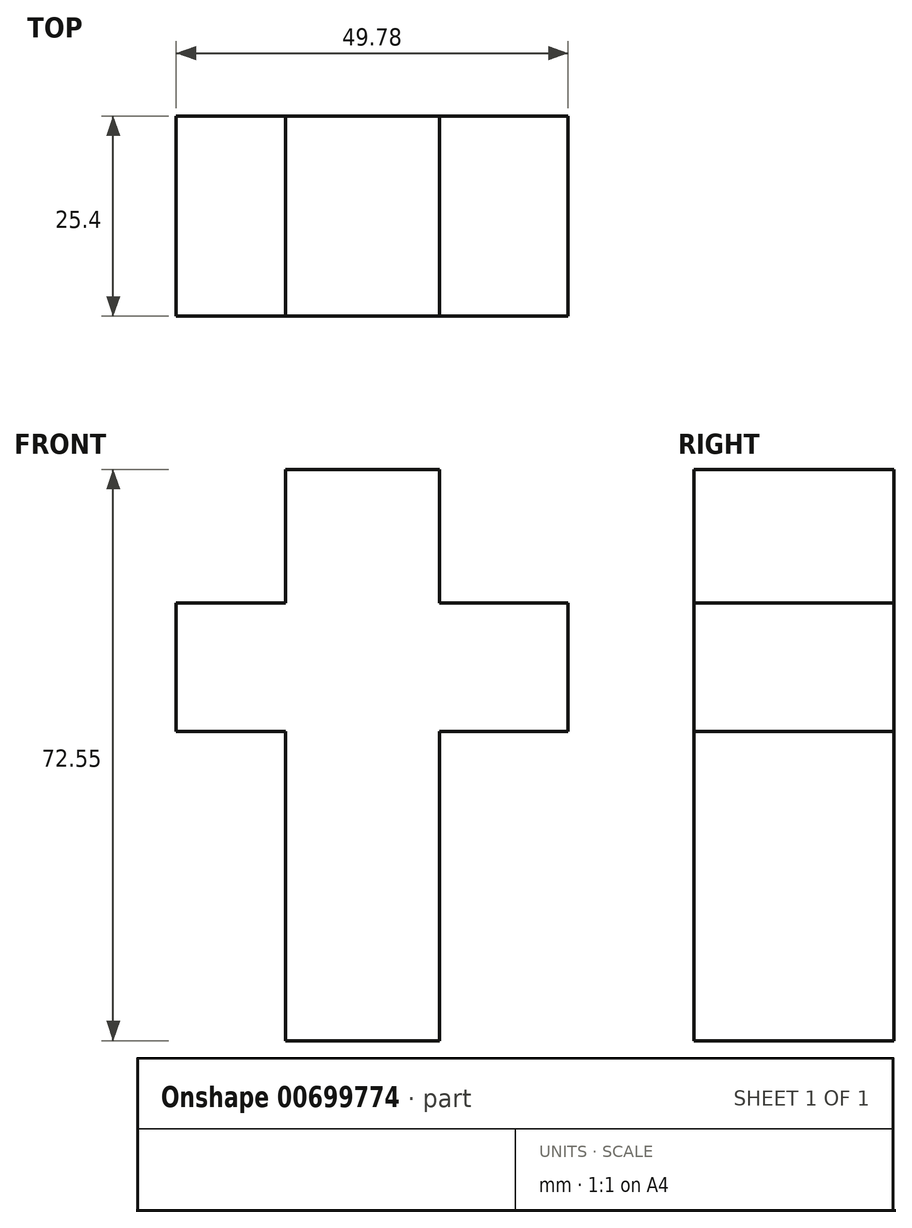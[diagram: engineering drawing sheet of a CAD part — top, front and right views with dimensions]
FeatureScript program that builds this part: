
annotation { "Feature Type Name" : "Feature", "Feature Type Description" : "" }
export const myFeature = defineFeature(function(context is Context, id is Id, definition is map)
    precondition{}
    {
        {
            var Q0;
            Q0=qCreatedBy(makeId("Front.planeOp"),FACE);
            var sketch = newSketch(context, id + "F0", { "sketchPlane" : qUnion([Q0])});
            skLineSegment(sketch, "E0", {"start": v(-29.12, 0) * mm, "end": v(-29.12, -22.87) * mm});
            skLineSegment(sketch, "E1", {"start": v(-29.12, -22.87) * mm, "end": v(-9.57, -22.87) * mm});
            skLineSegment(sketch, "E2", {"start": v(-9.57, -23.08) * mm, "end": v(-9.57, 0) * mm});
            skLineSegment(sketch, "E3", {"start": v(-9.57, 0) * mm, "end": v(-9.57, 16.43) * mm});
            skLineSegment(sketch, "E4", {"start": v(-9.57, 16.43) * mm, "end": v(6.75, 16.43) * mm});
            skLineSegment(sketch, "E5", {"start": v(6.75, 16.43) * mm, "end": v(6.75, 28.11) * mm});
            skLineSegment(sketch, "E6", {"start": v(6.75, 28.11) * mm, "end": v(6.75, 32.75) * mm});
            skLineSegment(sketch, "E7", {"start": v(6.75, 32.75) * mm, "end": v(-9.57, 32.75) * mm});
            skLineSegment(sketch, "E8", {"start": v(-9.57, 32.75) * mm, "end": v(-9.57, 49.68) * mm});
            skLineSegment(sketch, "E9", {"start": v(-9.57, 49.68) * mm, "end": v(-29.12, 49.68) * mm});
            skLineSegment(sketch, "E10", {"start": v(-29.12, 49.68) * mm, "end": v(-29.12, 32.75) * mm});
            skLineSegment(sketch, "E11", {"start": v(-29.12, 32.75) * mm, "end": v(-43.03, 32.75) * mm});
            skLineSegment(sketch, "E12", {"start": v(-43.03, 32.75) * mm, "end": v(-43.03, 16.43) * mm});
            skLineSegment(sketch, "E13", {"start": v(-43.03, 16.43) * mm, "end": v(-29.12, 16.43) * mm});
            skLineSegment(sketch, "E14", {"start": v(-29.12, 16.43) * mm, "end": v(-29.12, 0) * mm});
            skSolve(sketch);
        }
        {
            var Q0;
            Q0=makeQuery(id+"F0.imprint","IMPRINT",FACE,{"disambiguationData":[TD([[makeQuery(id+"F0.imprint","IMPRINT",EDGE,{"derivedFrom":sQuery(id+"F0.wireOp",EDGE,"E0")}),1.0]])]});
            extrude(context, id + "F1", {"entities" : qUnion([Q0]), "depth" : 25.4 * mm, "offsetDistance" : 25.4 * mm});
        }
    });
